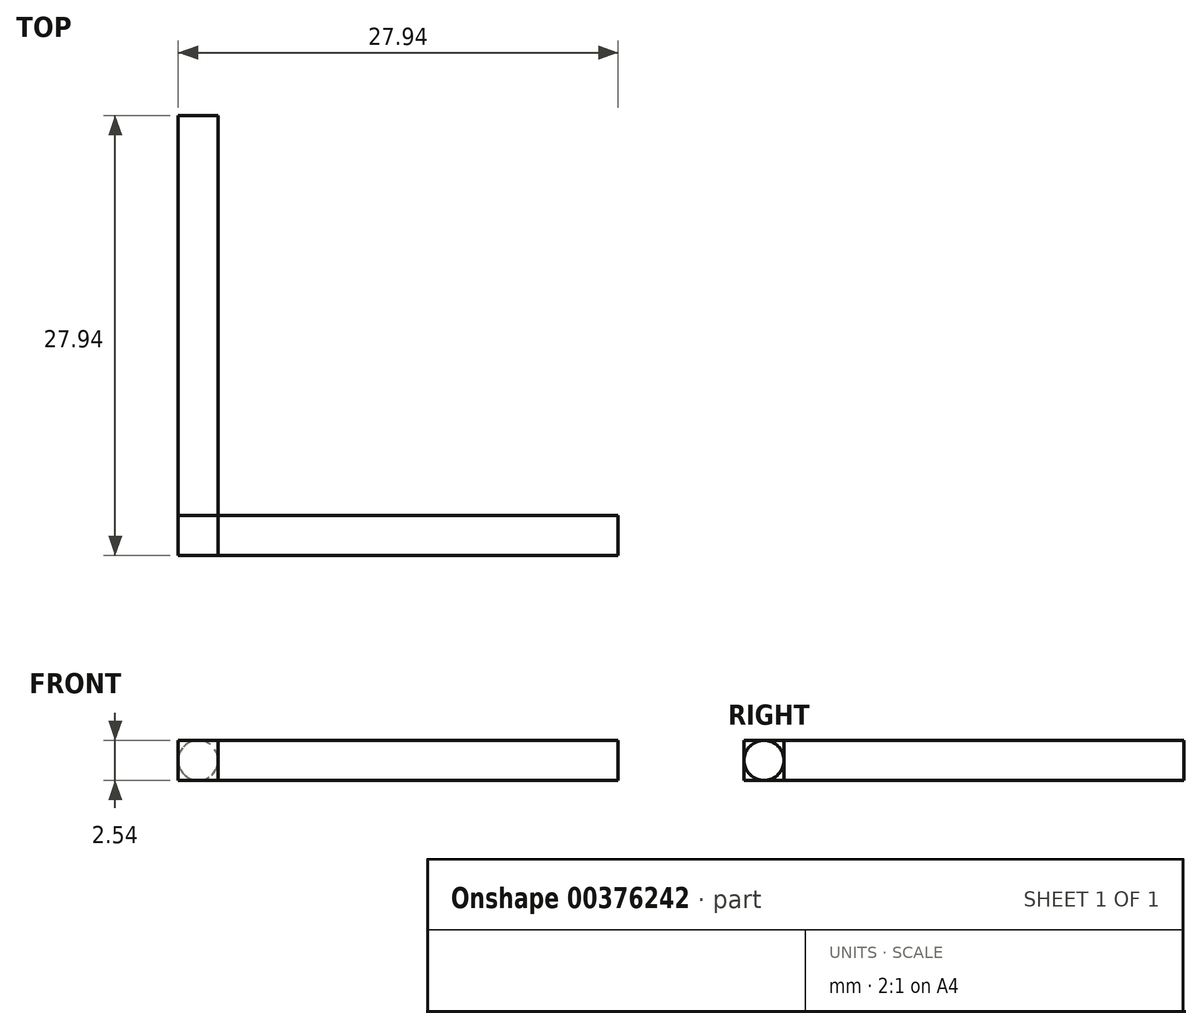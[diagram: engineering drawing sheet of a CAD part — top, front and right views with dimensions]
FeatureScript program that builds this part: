
annotation { "Feature Type Name" : "Feature", "Feature Type Description" : "" }
export const myFeature = defineFeature(function(context is Context, id is Id, definition is map)
    precondition{}
    {
        {
            var Q0;
            Q0=qCreatedBy(makeId("Front.planeOp"),FACE);
            var sketch = newSketch(context, id + "F0", { "sketchPlane" : qUnion([Q0])});
            skCircle(sketch, "E0", {"center": v(0, 0) * mm, "radius": 1.27 * mm});
            skSolve(sketch);
        }
        {
            var Q0;
            Q0=makeQuery(id+"F0.imprint","IMPRINT",FACE,{"disambiguationData":[TD([[makeQuery(id+"F0.imprint","IMPRINT",EDGE,{"derivedFrom":sQuery(id+"F0.wireOp",EDGE,"E0")}),1.0]])]});
            extrude(context, id + "F1", {"entities" : qUnion([Q0]), "depth" : 25.4 * mm});
        }
        {
            var Q0;
            Q0=makeQuery(id+"F1.opExtrude","CAP_FACE",FACE,{"disambiguationData":[OSD([sQuery(id+"F0.wireOp",EDGE,"E0")])],"isStart":false});
            var sketch = newSketch(context, id + "F2", { "sketchPlane" : qUnion([Q0])});
            skLineSegment(sketch, "E1.bottom", {"start": v(1.27, -1.27) * mm, "end": v(-1.27, -1.27) * mm});
            skLineSegment(sketch, "E1.top", {"start": v(1.27, 1.27) * mm, "end": v(-1.27, 1.27) * mm});
            skLineSegment(sketch, "E1.left", {"start": v(1.27, -1.27) * mm, "end": v(1.27, 1.27) * mm});
            skLineSegment(sketch, "E1.right", {"start": v(-1.27, -1.27) * mm, "end": v(-1.27, 1.27) * mm});
            skPoint(sketch, "E1.middle", {"position": v(0, 0) * mm});
            skSolve(sketch);
        }
        {
            var Q0;
            {var subQ0=makeQuery(id+"F1.opExtrude","CAP_EDGE",EDGE,{"disambiguationData":[OSD([sQuery(id+"F0.wireOp",EDGE,"E0")])],"isStart":false});var subQ1=makeQuery(id+"F2.imprint","INTERSECT",VERTEX,{"derivedFrom":[subQ0,sQuery(id+"F2.wireOp",EDGE,"E1.bottom")]});Q0=makeQuery(id+"F2.imprint","IMPRINT",FACE,{"disambiguationData":[TD([[makeQuery(id+"F2.imprint","IMPRINT",EDGE,{"disambiguationData":[TD([[subQ1,-1.0]])],"derivedFrom":subQ0}),1.0]])]});}
            var Q1;
            {var subQ0=sQuery(id+"F2.wireOp",EDGE,"E1.left");var subQ1=sQuery(id+"F2.wireOp",EDGE,"E1.top");var subQ2=makeQuery(id+"F2.imprint","INTERSECT",VERTEX,{"derivedFrom":[subQ1,subQ0]});Q1=makeQuery(id+"F2.imprint","IMPRINT",FACE,{"disambiguationData":[TD([[makeQuery(id+"F2.imprint","IMPRINT",EDGE,{"disambiguationData":[TD([[subQ2,-1.0]])],"derivedFrom":subQ1}),1.0]])]});}
            var Q2;
            {var subQ0=sQuery(id+"F2.wireOp",EDGE,"E1.left");var subQ1=sQuery(id+"F2.wireOp",EDGE,"E1.bottom");var subQ2=makeQuery(id+"F2.imprint","INTERSECT",VERTEX,{"derivedFrom":[subQ1,subQ0]});Q2=makeQuery(id+"F2.imprint","IMPRINT",FACE,{"disambiguationData":[TD([[makeQuery(id+"F2.imprint","IMPRINT",EDGE,{"disambiguationData":[TD([[subQ2,-1.0]])],"derivedFrom":subQ1}),-1.0]])]});}
            var Q3;
            {var subQ0=sQuery(id+"F2.wireOp",EDGE,"E1.right");var subQ1=sQuery(id+"F2.wireOp",EDGE,"E1.bottom");var subQ2=makeQuery(id+"F2.imprint","INTERSECT",VERTEX,{"derivedFrom":[subQ1,subQ0]});Q3=makeQuery(id+"F2.imprint","IMPRINT",FACE,{"disambiguationData":[TD([[makeQuery(id+"F2.imprint","IMPRINT",EDGE,{"disambiguationData":[TD([[subQ2,1.0]])],"derivedFrom":subQ1}),-1.0]])]});}
            var Q4;
            {var subQ0=sQuery(id+"F2.wireOp",EDGE,"E1.right");var subQ1=sQuery(id+"F2.wireOp",EDGE,"E1.top");var subQ2=makeQuery(id+"F2.imprint","INTERSECT",VERTEX,{"derivedFrom":[subQ1,subQ0]});Q4=makeQuery(id+"F2.imprint","IMPRINT",FACE,{"disambiguationData":[TD([[makeQuery(id+"F2.imprint","IMPRINT",EDGE,{"disambiguationData":[TD([[subQ2,1.0]])],"derivedFrom":subQ1}),1.0]])]});}
            extrude(context, id + "F3", {"entities" : qUnion([Q0, Q1, Q2, Q3, Q4]), "operationType" : NewBodyOperationType.ADD, "depth" : 2.54 * mm});
        }
        {
            var Q0;
            Q0=makeQuery(id+"F3.opExtrude","SWEPT_FACE",FACE,{"disambiguationData":[OSD([sQuery(id+"F2.wireOp",EDGE,"E1.left")])]});
            var sketch = newSketch(context, id + "F4", { "sketchPlane" : qUnion([Q0])});
            skLineSegment(sketch, "E2", {"start": v(-25.4, 0) * mm, "end": v(-27.94, 0) * mm});
            skCircle(sketch, "E3", {"center": v(-26.67, 0) * mm, "radius": 1.27 * mm});
            skSolve(sketch);
        }
        {
            var Q0;
            {var subQ0=sQuery(id+"F4.wireOp",EDGE,"E2");Q0=makeQuery(id+"F4.imprint","IMPRINT",FACE,{"disambiguationData":[TD([[makeQuery(id+"F4.imprint","IMPRINT",EDGE,{"derivedFrom":subQ0}),-1.0]])]});}
            var Q1;
            {var subQ0=sQuery(id+"F4.wireOp",EDGE,"E2");Q1=makeQuery(id+"F4.imprint","IMPRINT",FACE,{"disambiguationData":[TD([[makeQuery(id+"F4.imprint","IMPRINT",EDGE,{"derivedFrom":subQ0}),1.0]])]});}
            extrude(context, id + "F5", {"entities" : qUnion([Q0, Q1]), "operationType" : NewBodyOperationType.ADD, "depth" : 25.4 * mm});
        }
    });
